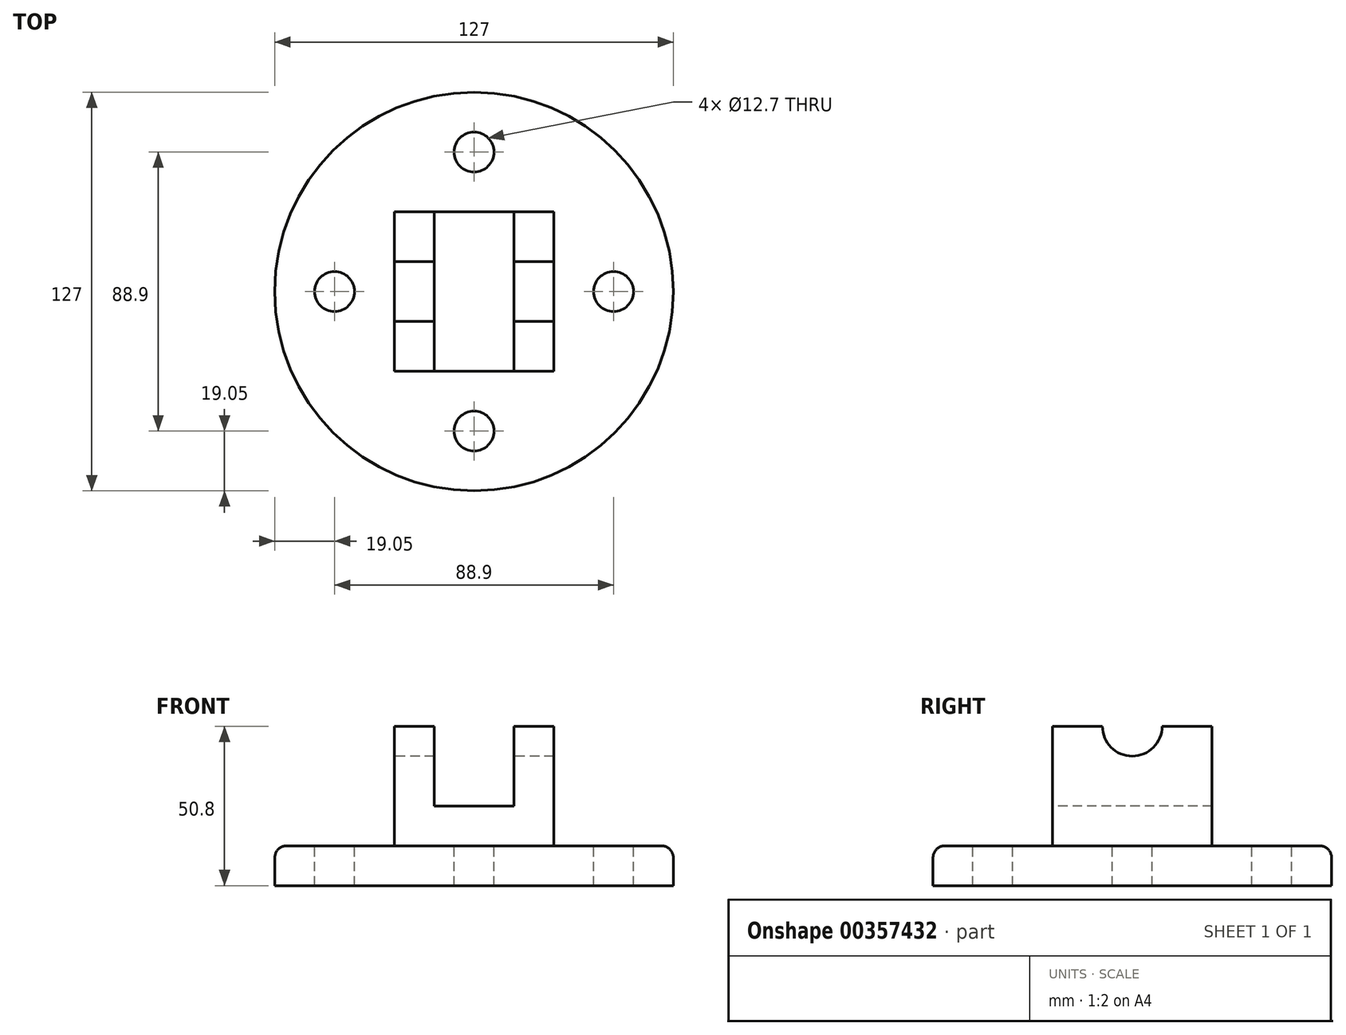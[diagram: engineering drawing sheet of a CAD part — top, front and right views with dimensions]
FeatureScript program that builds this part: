
annotation { "Feature Type Name" : "Feature", "Feature Type Description" : "" }
export const myFeature = defineFeature(function(context is Context, id is Id, definition is map)
    precondition{}
    {
        {
            var Q0;
            Q0=qCreatedBy(makeId("Top.planeOp"),FACE);
            var sketch = newSketch(context, id + "F0", { "sketchPlane" : qUnion([Q0])});
            skCircle(sketch, "E0", {"center": v(0, 0) * mm, "radius": 63.5 * mm});
            skCircle(sketch, "E1", {"center": v(0, 0) * mm, "radius": 44.45 * mm, "construction": true});
            skCircle(sketch, "E2", {"center": v(0, 44.45) * mm, "radius": 6.35 * mm});
            skCircle(sketch, "E3", {"center": v(44.45, 0) * mm, "radius": 6.35 * mm});
            skCircle(sketch, "E4", {"center": v(0, -44.45) * mm, "radius": 6.35 * mm});
            skCircle(sketch, "E5", {"center": v(-44.45, 0) * mm, "radius": 6.35 * mm});
            skSolve(sketch);
        }
        {
            var Q0;
            Q0=makeQuery(id+"F0.imprint","IMPRINT",FACE,{"disambiguationData":[TD([[makeQuery(id+"F0.imprint","IMPRINT",EDGE,{"derivedFrom":sQuery(id+"F0.wireOp",EDGE,"E0")}),1.0]])]});
            extrude(context, id + "F1", {"entities" : qUnion([Q0]), "oppositeDirection" : true, "depth" : 12.7 * mm});
        }
        {
            var Q0;
            Q0=qCreatedBy(makeId("Right.planeOp"),FACE);
            var sketch = newSketch(context, id + "F2", { "sketchPlane" : qUnion([Q0])});
            skLineSegment(sketch, "E6", {"start": v(-25.4, 0) * mm, "end": v(25.4, 0) * mm});
            skLineSegment(sketch, "E7", {"start": v(25.4, 0) * mm, "end": v(25.4, 38.1) * mm});
            skLineSegment(sketch, "E8", {"start": v(0, 50.33) * mm, "end": v(0, -49.36) * mm, "construction": true});
            skLineSegment(sketch, "E9", {"start": v(-25.4, 0) * mm, "end": v(-25.4, 38.1) * mm});
            skArc(sketch, "E10", {"start": v(-25.4, 38.1) * mm, "mid": v(0, 63.5) * mm, "end": v(25.4, 38.1) * mm});
            skCircle(sketch, "E11", {"center": v(0, 38.1) * mm, "radius": 9.53 * mm});
            skSolve(sketch);
        }
        {
            var Q0;
            Q0=makeQuery(id+"F2.imprint","IMPRINT",FACE,{"disambiguationData":[TD([[makeQuery(id+"F2.imprint","IMPRINT",EDGE,{"derivedFrom":sQuery(id+"F2.wireOp",EDGE,"E6")}),1.0]])]});
            extrude(context, id + "F3", {"entities" : qUnion([Q0]), "operationType" : NewBodyOperationType.ADD, "endBound" : BoundingType.SYMMETRIC, "depth" : 50.8 * mm});
        }
        {
            var Q0;
            Q0=makeQuery(id+"F3.opExtrude","SWEPT_FACE",FACE,{"disambiguationData":[OSD([sQuery(id+"F2.wireOp",EDGE,"E9")])]});
            var sketch = newSketch(context, id + "F4", { "sketchPlane" : qUnion([Q0])});
            skLineSegment(sketch, "E12.bottom", {"start": v(-25.4, 63.5) * mm, "end": v(25.4, 63.5) * mm});
            skLineSegment(sketch, "E12.top", {"start": v(-25.4, 0) * mm, "end": v(25.4, 0) * mm});
            skLineSegment(sketch, "E12.left", {"start": v(-25.4, 63.5) * mm, "end": v(-25.4, 0) * mm});
            skLineSegment(sketch, "E12.right", {"start": v(25.4, 63.5) * mm, "end": v(25.4, 0) * mm});
            skLineSegment(sketch, "E13", {"start": v(-25.4, 63.5) * mm, "end": v(-12.7, 63.5) * mm});
            skLineSegment(sketch, "E14", {"start": v(0, 0) * mm, "end": v(0, 90.01) * mm, "construction": true});
            skLineSegment(sketch, "E15", {"start": v(-12.7, 63.5) * mm, "end": v(-12.7, 12.7) * mm});
            skLineSegment(sketch, "E16", {"start": v(-12.7, 12.7) * mm, "end": v(12.7, 12.7) * mm});
            skLineSegment(sketch, "E17", {"start": v(12.7, 12.7) * mm, "end": v(12.7, 63.5) * mm});
            skLineSegment(sketch, "E18", {"start": v(12.7, 63.5) * mm, "end": v(25.4, 63.5) * mm});
            skLineSegment(sketch, "E19.trimOffspring", {"start": v(0, 63.5) * mm, "end": v(25.4, 63.5) * mm});
            skSolve(sketch);
        }
        {
            var Q0;
            {var subQ1=sQuery(id+"F4.wireOp",EDGE,"E12.bottom");Q0=makeQuery(id+"F4.imprint","IMPRINT",FACE,{"disambiguationData":[TD([[makeQuery(id+"F4.imprint","IMPRINT",EDGE,{"derivedFrom":subQ1}),-1.0]])]});}
            var Q1;
            {var subQ0=sQuery(id+"F4.wireOp",EDGE,"E16");Q1=makeQuery(id+"F4.imprint","IMPRINT",FACE,{"disambiguationData":[TD([[makeQuery(id+"F4.imprint","IMPRINT",EDGE,{"derivedFrom":subQ0}),1.0]])]});}
            extrude(context, id + "F5", {"entities" : qUnion([Q0, Q1]), "operationType" : NewBodyOperationType.REMOVE, "endBound" : BoundingType.THROUGH_ALL, "oppositeDirection" : true, "depth" : 25.4 * mm});
        }
        {
            var Q0;
            Q0=makeQuery(id+"F3.opExtrude","SWEPT_EDGE",EDGE,{"disambiguationData":[OSD([sQuery(id+"F2.wireOp",EDGE,"E6"),sQuery(id+"F2.wireOp",EDGE,"E9")])]});
            var Q1;
            Q1=makeQuery(id+"F3.opExtrude","CAP_EDGE",EDGE,{"disambiguationData":[OSD([sQuery(id+"F2.wireOp",EDGE,"E6")])],"isStart":false});
            var Q2;
            Q2=makeQuery(id+"F3.opExtrude","CAP_EDGE",EDGE,{"disambiguationData":[OSD([sQuery(id+"F2.wireOp",EDGE,"E6")])],"isStart":true});
            var Q3;
            Q3=makeQuery(id+"F3.opExtrude","SWEPT_EDGE",EDGE,{"disambiguationData":[OSD([sQuery(id+"F2.wireOp",EDGE,"E6"),sQuery(id+"F2.wireOp",EDGE,"E7")])]});
            var Q4;
            Q4=makeQuery(id+"F1.opExtrude","CAP_EDGE",EDGE,{"disambiguationData":[OSD([sQuery(id+"F0.wireOp",EDGE,"E0")])],"isStart":true});
            fillet(context, id + "F6", {"entities" : qUnion([Q0, Q1, Q2, Q3, Q4]), "radius" : 3.8 * mm, "tangentPropagation" : true, "allowEdgeOverflow" : false});
        }
    });
